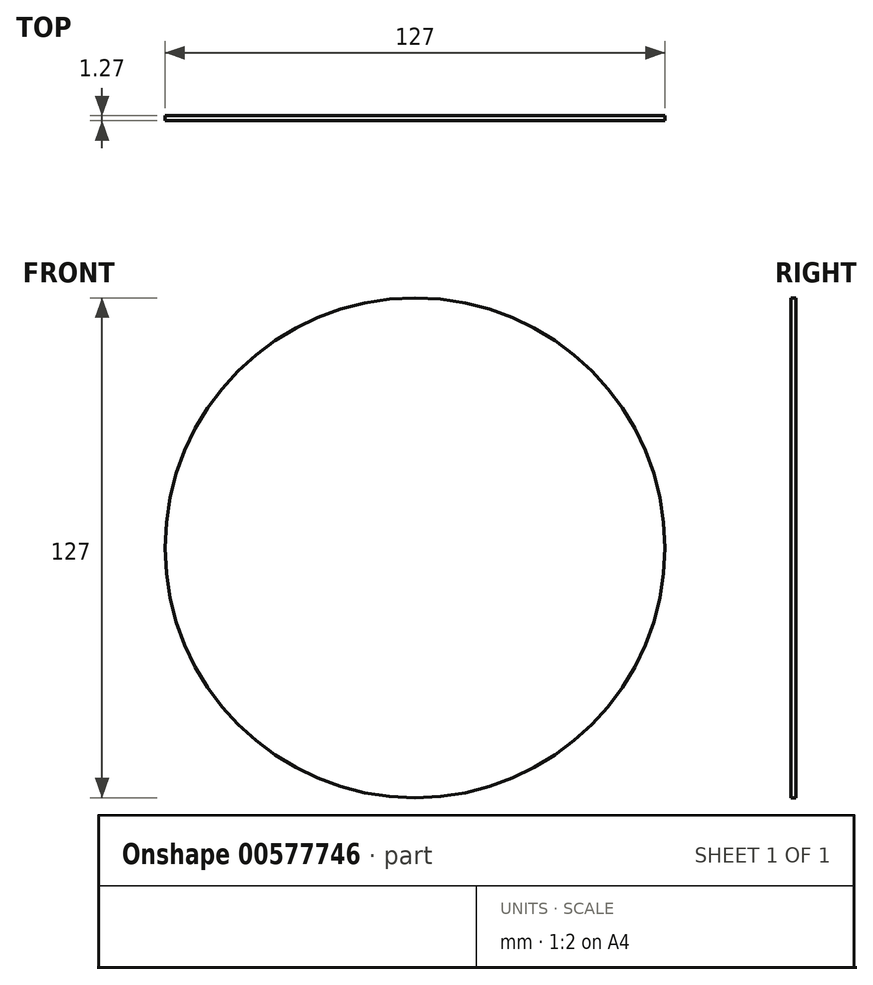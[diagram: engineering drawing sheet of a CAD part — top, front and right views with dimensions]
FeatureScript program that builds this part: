
annotation { "Feature Type Name" : "Feature", "Feature Type Description" : "" }
export const myFeature = defineFeature(function(context is Context, id is Id, definition is map)
    precondition{}
    {
        {
            var Q0;
            Q0=qCreatedBy(makeId("Front.planeOp"),FACE);
            var sketch = newSketch(context, id + "F0", { "sketchPlane" : qUnion([Q0])});
            skCircle(sketch, "E0", {"center": v(0, 0) * mm, "radius": 63.5 * mm});
            skSolve(sketch);
        }
        {
            var Q0;
            Q0=makeQuery(id+"F0.imprint","IMPRINT",FACE,{"disambiguationData":[TD([[makeQuery(id+"F0.imprint","IMPRINT",EDGE,{"derivedFrom":sQuery(id+"F0.wireOp",EDGE,"E0")}),1.0]])]});
            extrude(context, id + "F1", {"entities" : qUnion([Q0]), "depth" : 1.27 * mm, "offsetDistance" : 25.4 * mm});
        }
    });
